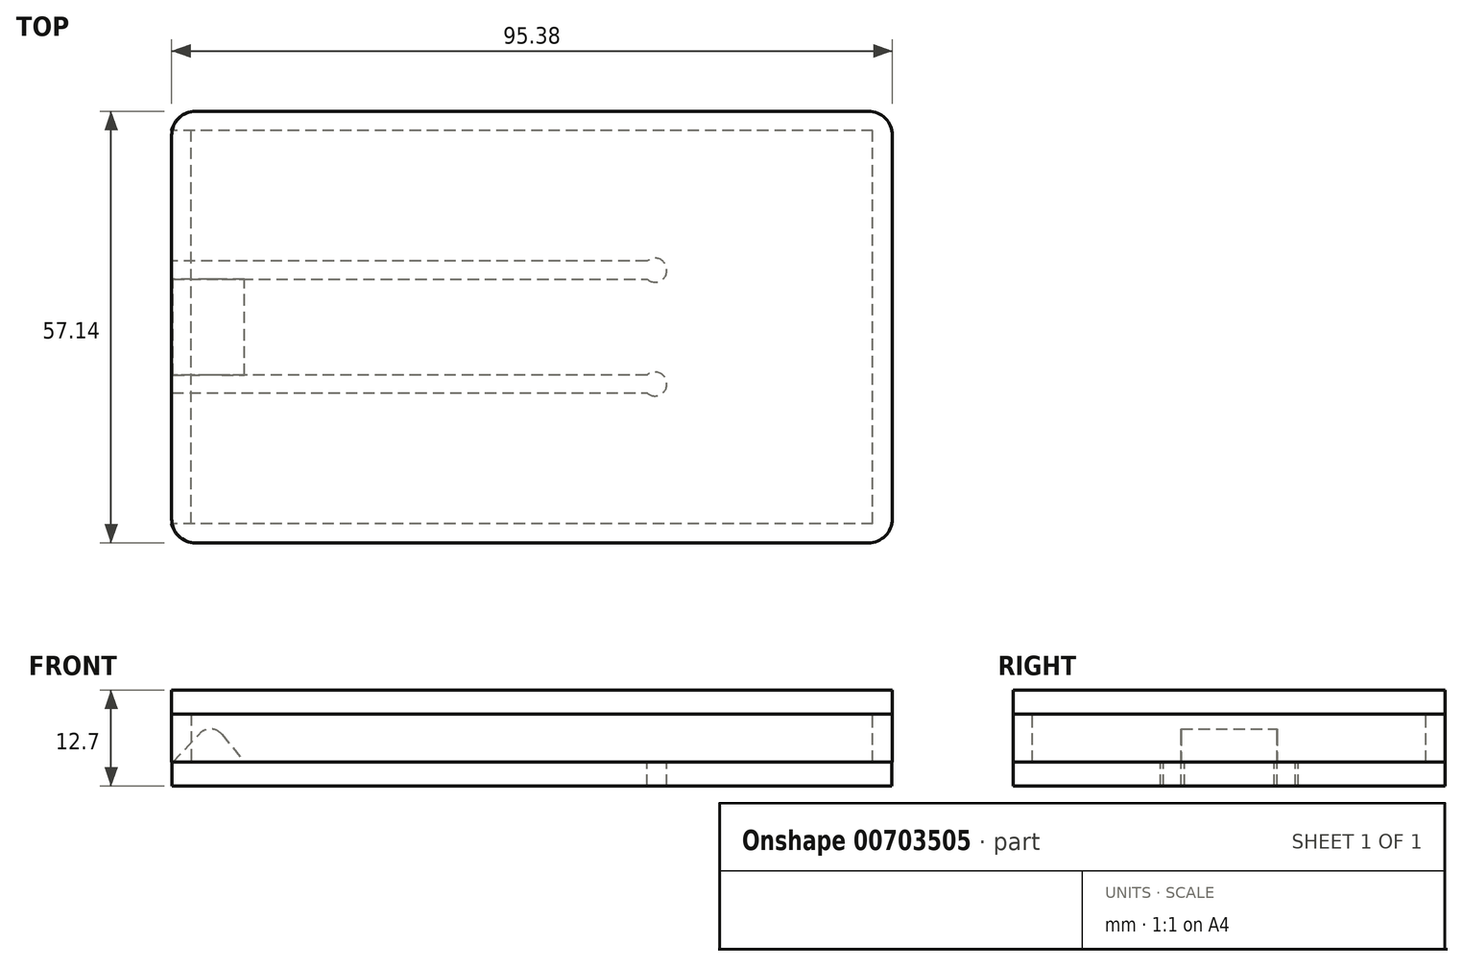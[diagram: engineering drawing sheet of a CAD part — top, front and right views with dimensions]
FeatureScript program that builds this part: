
annotation { "Feature Type Name" : "Feature", "Feature Type Description" : "" }
export const myFeature = defineFeature(function(context is Context, id is Id, definition is map)
    precondition{}
    {
        {
            var Q0;
            Q0=qCreatedBy(makeId("Top.planeOp"),FACE);
            var sketch = newSketch(context, id + "F0", { "sketchPlane" : qUnion([Q0])});
            skLineSegment(sketch, "E0.bottom", {"start": v(45.09, -26.03) * mm, "end": v(-45.09, -26.04) * mm});
            skLineSegment(sketch, "E0.top", {"start": v(45.09, 26.04) * mm, "end": v(-45.09, 26.03) * mm});
            skLineSegment(sketch, "E0.left", {"start": v(45.09, -26.03) * mm, "end": v(45.09, 26.04) * mm});
            skLineSegment(sketch, "E0.right", {"start": v(-45.09, -26.04) * mm, "end": v(-45.09, 26.03) * mm});
            skPoint(sketch, "E0.middle", {"position": v(0, 0) * mm});
            skSolve(sketch);
        }
        {
            var Q0;
            Q0=makeQuery(id+"F0.imprint","IMPRINT",FACE,{"disambiguationData":[TD([[makeQuery(id+"F0.imprint","IMPRINT",EDGE,{"derivedFrom":sQuery(id+"F0.wireOp",EDGE,"E0.bottom")}),-1.0]])]});
            extrude(context, id + "F1", {"entities" : qUnion([Q0]), "depth" : 6.35 * mm, "offsetDistance" : 25.4 * mm});
        }
        {
            var Q0;
            Q0=makeQuery(id+"F1.opExtrude","CAP_FACE",FACE,{"disambiguationData":[OSD([sQuery(id+"F0.wireOp",EDGE,"E0.bottom"),sQuery(id+"F0.wireOp",EDGE,"E0.top"),sQuery(id+"F0.wireOp",EDGE,"E0.left"),sQuery(id+"F0.wireOp",EDGE,"E0.right")])],"isStart":false});
            var sketch = newSketch(context, id + "F2", { "sketchPlane" : qUnion([Q0])});
            skLineSegment(sketch, "E1.bottom", {"start": v(47.69, 28.58) * mm, "end": v(-47.69, 28.58) * mm});
            skLineSegment(sketch, "E1.top", {"start": v(47.69, -28.58) * mm, "end": v(-47.69, -28.58) * mm});
            skLineSegment(sketch, "E1.left", {"start": v(47.69, 28.58) * mm, "end": v(47.69, -28.58) * mm});
            skLineSegment(sketch, "E1.right", {"start": v(-47.69, 28.58) * mm, "end": v(-47.69, -28.58) * mm});
            skPoint(sketch, "E1.middle", {"position": v(0, 0) * mm});
            skSolve(sketch);
        }
        {
            var Q0;
            Q0=makeQuery(id+"F2.imprint","IMPRINT",FACE,{"disambiguationData":[TD([[makeQuery(id+"F2.imprint","IMPRINT",EDGE,{"derivedFrom":sQuery(id+"F2.wireOp",EDGE,"E1.bottom")}),1.0]])]});
            var Q1;
            Q1=makeQuery(id+"F2.imprint","IMPRINT",FACE,{"disambiguationData":[TD([[makeQuery(id+"F2.imprint","IMPRINT",EDGE,{"derivedFrom":makeQuery(id+"F1.opExtrude","CAP_EDGE",EDGE,{"disambiguationData":[OSD([sQuery(id+"F0.wireOp",EDGE,"E0.bottom")])],"isStart":false})}),-1.0]])]});
            extrude(context, id + "F3", {"entities" : qUnion([Q0, Q1]), "depth" : 3.17 * mm, "offsetDistance" : 25.4 * mm});
        }
        {
            var Q0;
            Q0=makeQuery(id+"F1.opExtrude","CAP_FACE",FACE,{"disambiguationData":[OSD([sQuery(id+"F0.wireOp",EDGE,"E0.bottom"),sQuery(id+"F0.wireOp",EDGE,"E0.top"),sQuery(id+"F0.wireOp",EDGE,"E0.left"),sQuery(id+"F0.wireOp",EDGE,"E0.right")])],"isStart":true});
            var sketch = newSketch(context, id + "F4", { "sketchPlane" : qUnion([Q0])});
            skLineSegment(sketch, "E2.bottom", {"start": v(-47.62, 28.58) * mm, "end": v(47.63, 28.58) * mm});
            skLineSegment(sketch, "E2.top", {"start": v(-47.62, -28.58) * mm, "end": v(47.62, -28.58) * mm});
            skLineSegment(sketch, "E2.left", {"start": v(-47.62, 28.58) * mm, "end": v(-47.63, 8.73) * mm});
            skLineSegment(sketch, "E2.right", {"start": v(47.63, 28.58) * mm, "end": v(47.62, -28.57) * mm});
            skPoint(sketch, "E2.middle", {"position": v(0, 0) * mm});
            skLineSegment(sketch, "E3", {"start": v(-47.63, 8.73) * mm, "end": v(15.21, 8.73) * mm});
            skLineSegment(sketch, "E4", {"start": v(15.21, 6.35) * mm, "end": v(-47.63, 6.35) * mm});
            skLineSegment(sketch, "E5", {"start": v(-47.62, -6.35) * mm, "end": v(15.21, -6.35) * mm});
            skLineSegment(sketch, "E6", {"start": v(15.21, -8.73) * mm, "end": v(-47.63, -8.73) * mm});
            skLineSegment(sketch, "E7.trimOffspring", {"start": v(-47.63, 6.35) * mm, "end": v(-47.63, -6.35) * mm});
            skLineSegment(sketch, "E8.trimOffspring", {"start": v(-47.63, -8.73) * mm, "end": v(-47.63, -28.57) * mm});
            skArc(sketch, "E9", {"start": v(15.21, 6.35) * mm, "mid": v(17.85, 7.54) * mm, "end": v(15.21, 8.73) * mm});
            skArc(sketch, "E10", {"start": v(15.21, -8.73) * mm, "mid": v(17.85, -7.54) * mm, "end": v(15.21, -6.35) * mm});
            skPoint(sketch, "E11.orphan", {"position": v(16.26, 8.73) * mm});
            skPoint(sketch, "E12.orphan", {"position": v(16.26, 6.35) * mm});
            skPoint(sketch, "E13.orphan", {"position": v(16.26, -6.35) * mm});
            skPoint(sketch, "E14.orphan", {"position": v(16.26, -8.73) * mm});
            skSolve(sketch);
        }
        {
            var Q0;
            Q0=makeQuery(id+"F4.imprint","IMPRINT",FACE,{"disambiguationData":[TD([[makeQuery(id+"F4.imprint","IMPRINT",EDGE,{"derivedFrom":sQuery(id+"F4.wireOp",EDGE,"E2.bottom")}),-1.0]])]});
            var Q1;
            {var subQ5=sQuery(id+"F4.wireOp",EDGE,"E9");Q1=makeQuery(id+"F4.imprint","IMPRINT",FACE,{"disambiguationData":[TD([[makeQuery(id+"F4.imprint","IMPRINT",EDGE,{"derivedFrom":subQ5}),-1.0]])]});}
            var Q2;
            {var subQ0=sQuery(id+"F4.wireOp",EDGE,"E7.trimOffspring");Q2=makeQuery(id+"F4.imprint","IMPRINT",FACE,{"disambiguationData":[TD([[makeQuery(id+"F4.imprint","IMPRINT",EDGE,{"derivedFrom":subQ0}),1.0]])]});}
            extrude(context, id + "F5", {"entities" : qUnion([Q0, Q1, Q2]), "depth" : 3.17 * mm, "offsetDistance" : 25.4 * mm});
        }
        {
            var Q0;
            Q0=makeQuery(id+"F3.opExtrude","CAP_FACE",FACE,{"disambiguationData":[OSD([sQuery(id+"F2.wireOp",EDGE,"E1.bottom"),sQuery(id+"F2.wireOp",EDGE,"E1.top"),sQuery(id+"F2.wireOp",EDGE,"E1.left"),sQuery(id+"F2.wireOp",EDGE,"E1.right")])],"isStart":true});
            var sketch = newSketch(context, id + "F6", { "sketchPlane" : qUnion([Q0])});
            skLineSegment(sketch, "E15.bottom", {"start": v(-41.54, 26.68) * mm, "end": v(41.54, 26.68) * mm});
            skLineSegment(sketch, "E15.top", {"start": v(-41.54, -23.39) * mm, "end": v(41.54, -23.39) * mm});
            skLineSegment(sketch, "E15.left", {"start": v(-41.54, 26.68) * mm, "end": v(-41.54, -23.39) * mm});
            skLineSegment(sketch, "E15.right", {"start": v(41.54, 26.68) * mm, "end": v(41.54, -23.39) * mm});
            skPoint(sketch, "E15.middle", {"position": v(0, 1.65) * mm});
            skSolve(sketch);
        }
        {
            var Q0;
            Q0=makeQuery(id+"F6.imprint","IMPRINT",FACE,{"disambiguationData":[TD([[makeQuery(id+"F6.imprint","IMPRINT",EDGE,{"derivedFrom":sQuery(id+"F6.wireOp",EDGE,"E15.bottom")}),1.0]])]});
            var sketch = newSketch(context, id + "F7", { "sketchPlane" : qUnion([Q0])});
            skLineSegment(sketch, "E16.bottom", {"start": v(-47.69, 28.58) * mm, "end": v(47.69, 28.58) * mm});
            skLineSegment(sketch, "E16.top", {"start": v(-47.69, -28.58) * mm, "end": v(47.69, -28.58) * mm});
            skLineSegment(sketch, "E16.left", {"start": v(-47.69, 28.58) * mm, "end": v(-47.69, 26.04) * mm});
            skLineSegment(sketch, "E16.right", {"start": v(47.69, 28.58) * mm, "end": v(47.69, -28.58) * mm});
            skPoint(sketch, "E16.middle", {"position": v(0, 0) * mm});
            skLineSegment(sketch, "E17.0", {"start": v(45.09, -26.04) * mm, "end": v(-45.09, -26.03) * mm});
            skLineSegment(sketch, "E18.0", {"start": v(45.09, 26.03) * mm, "end": v(-45.09, 26.04) * mm});
            skLineSegment(sketch, "E19.0", {"start": v(45.09, 26.04) * mm, "end": v(45.09, -26.04) * mm});
            skLineSegment(sketch, "E20", {"start": v(-45.09, 26.04) * mm, "end": v(-47.69, 26.04) * mm});
            skLineSegment(sketch, "E21", {"start": v(-45.09, -26.03) * mm, "end": v(-47.69, -26.03) * mm});
            skLineSegment(sketch, "E22.trimOffspring", {"start": v(-47.69, -26.03) * mm, "end": v(-47.69, -28.58) * mm});
            skSolve(sketch);
        }
        {
            var Q0;
            Q0 = qSketchRegion(id + "F7", true);
            var Q1;
            Q1=makeQuery(id+"F5.opExtrude","CAP_FACE",FACE,{"disambiguationData":[OSD([sQuery(id+"F4.wireOp",EDGE,"E2.bottom"),sQuery(id+"F4.wireOp",EDGE,"E2.top"),sQuery(id+"F4.wireOp",EDGE,"E2.left"),sQuery(id+"F4.wireOp",EDGE,"E2.right"),sQuery(id+"F4.wireOp",EDGE,"E3"),sQuery(id+"F4.wireOp",EDGE,"E4"),sQuery(id+"F4.wireOp",EDGE,"E5"),sQuery(id+"F4.wireOp",EDGE,"E6"),sQuery(id+"F4.wireOp",EDGE,"E7.trimOffspring"),sQuery(id+"F4.wireOp",EDGE,"E8.trimOffspring"),sQuery(id+"F4.wireOp",EDGE,"E9"),sQuery(id+"F4.wireOp",EDGE,"E10")])],"isStart":true});
            extrude(context, id + "F8", {"entities" : qUnion([Q0]), "endBound" : BoundingType.UP_TO_SURFACE, "depth" : 25.4 * mm, "endBoundEntityFace" : qUnion([Q1]), "offsetDistance" : 25.4 * mm});
        }
        {
            var Q0;
            Q0=qCreatedBy(makeId("Front.planeOp"),FACE);
            var sketch = newSketch(context, id + "F9", { "sketchPlane" : qUnion([Q0])});
            skLineSegment(sketch, "E23", {"start": v(-47.5, 0) * mm, "end": v(-42.44, 5.4) * mm});
            skLineSegment(sketch, "E24", {"start": v(-42.44, 5.4) * mm, "end": v(-38.06, 0) * mm});
            skLineSegment(sketch, "E25", {"start": v(-38.06, 0) * mm, "end": v(-47.5, 0) * mm});
            skSolve(sketch);
        }
        {
            var Q0;
            Q0=makeQuery(id+"F9.imprint","IMPRINT",FACE,{"disambiguationData":[TD([[makeQuery(id+"F9.imprint","IMPRINT",EDGE,{"derivedFrom":sQuery(id+"F9.wireOp",EDGE,"E23")}),-1.0]])]});
            extrude(context, id + "F10", {"entities" : qUnion([Q0]), "endBound" : BoundingType.SYMMETRIC, "depth" : 12.7 * mm, "offsetDistance" : 25.4 * mm});
        }
        {
            var Q0;
            Q0=makeQuery(id+"F10.opExtrude","SWEPT_EDGE",EDGE,{"disambiguationData":[OSD([sQuery(id+"F9.wireOp",EDGE,"E23"),sQuery(id+"F9.wireOp",EDGE,"E24")])]});
            fillet(context, id + "F11", {"entities" : qUnion([Q0]), "radius" : 1.94 * mm, "tangentPropagation" : true, "allowEdgeOverflow" : false});
        }
        {
            var Q0;
            Q0=makeQuery(id+"F8.opExtrude","SWEPT_EDGE",EDGE,{"disambiguationData":[OSD([sQuery(id+"F7.wireOp",EDGE,"E16.bottom"),sQuery(id+"F7.wireOp",EDGE,"E16.left")])]});
            var Q1;
            Q1=makeQuery(id+"F3.opExtrude","SWEPT_EDGE",EDGE,{"disambiguationData":[OSD([sQuery(id+"F2.wireOp",EDGE,"E1.top"),sQuery(id+"F2.wireOp",EDGE,"E1.right")])]});
            var Q2;
            Q2=makeQuery(id+"F5.opExtrude","SWEPT_EDGE",EDGE,{"disambiguationData":[OSD([sQuery(id+"F4.wireOp",EDGE,"E2.bottom"),sQuery(id+"F4.wireOp",EDGE,"E2.left")])]});
            var Q3;
            Q3=makeQuery(id+"F3.opExtrude","SWEPT_EDGE",EDGE,{"disambiguationData":[OSD([sQuery(id+"F2.wireOp",EDGE,"E1.top"),sQuery(id+"F2.wireOp",EDGE,"E1.left")])]});
            var Q4;
            Q4=makeQuery(id+"F8.opExtrude","SWEPT_EDGE",EDGE,{"disambiguationData":[OSD([sQuery(id+"F7.wireOp",EDGE,"E16.bottom"),sQuery(id+"F7.wireOp",EDGE,"E16.right")])]});
            var Q5;
            Q5=makeQuery(id+"F5.opExtrude","SWEPT_EDGE",EDGE,{"disambiguationData":[OSD([sQuery(id+"F4.wireOp",EDGE,"E2.bottom"),sQuery(id+"F4.wireOp",EDGE,"E2.right")])]});
            var Q6;
            Q6=makeQuery(id+"F3.opExtrude","SWEPT_EDGE",EDGE,{"disambiguationData":[OSD([sQuery(id+"F2.wireOp",EDGE,"E1.bottom"),sQuery(id+"F2.wireOp",EDGE,"E1.left")])]});
            var Q7;
            Q7=makeQuery(id+"F8.opExtrude","SWEPT_EDGE",EDGE,{"disambiguationData":[OSD([sQuery(id+"F7.wireOp",EDGE,"E16.top"),sQuery(id+"F7.wireOp",EDGE,"E16.right")])]});
            var Q8;
            Q8=makeQuery(id+"F5.opExtrude","SWEPT_EDGE",EDGE,{"disambiguationData":[OSD([sQuery(id+"F4.wireOp",EDGE,"E2.top"),sQuery(id+"F4.wireOp",EDGE,"E2.right")])]});
            var Q9;
            Q9=makeQuery(id+"F3.opExtrude","SWEPT_EDGE",EDGE,{"disambiguationData":[OSD([sQuery(id+"F2.wireOp",EDGE,"E1.bottom"),sQuery(id+"F2.wireOp",EDGE,"E1.right")])]});
            var Q10;
            Q10=makeQuery(id+"F8.opExtrude","SWEPT_EDGE",EDGE,{"disambiguationData":[OSD([sQuery(id+"F7.wireOp",EDGE,"E16.top"),sQuery(id+"F7.wireOp",EDGE,"E22.trimOffspring")])]});
            var Q11;
            Q11=makeQuery(id+"F5.opExtrude","SWEPT_EDGE",EDGE,{"disambiguationData":[OSD([sQuery(id+"F4.wireOp",EDGE,"E2.top"),sQuery(id+"F4.wireOp",EDGE,"E8.trimOffspring")])]});
            fillet(context, id + "F12", {"entities" : qUnion([Q0, Q1, Q2, Q3, Q4, Q5, Q6, Q7, Q8, Q9, Q10, Q11]), "radius" : 3.17 * mm, "tangentPropagation" : true, "allowEdgeOverflow" : false});
        }
    });
